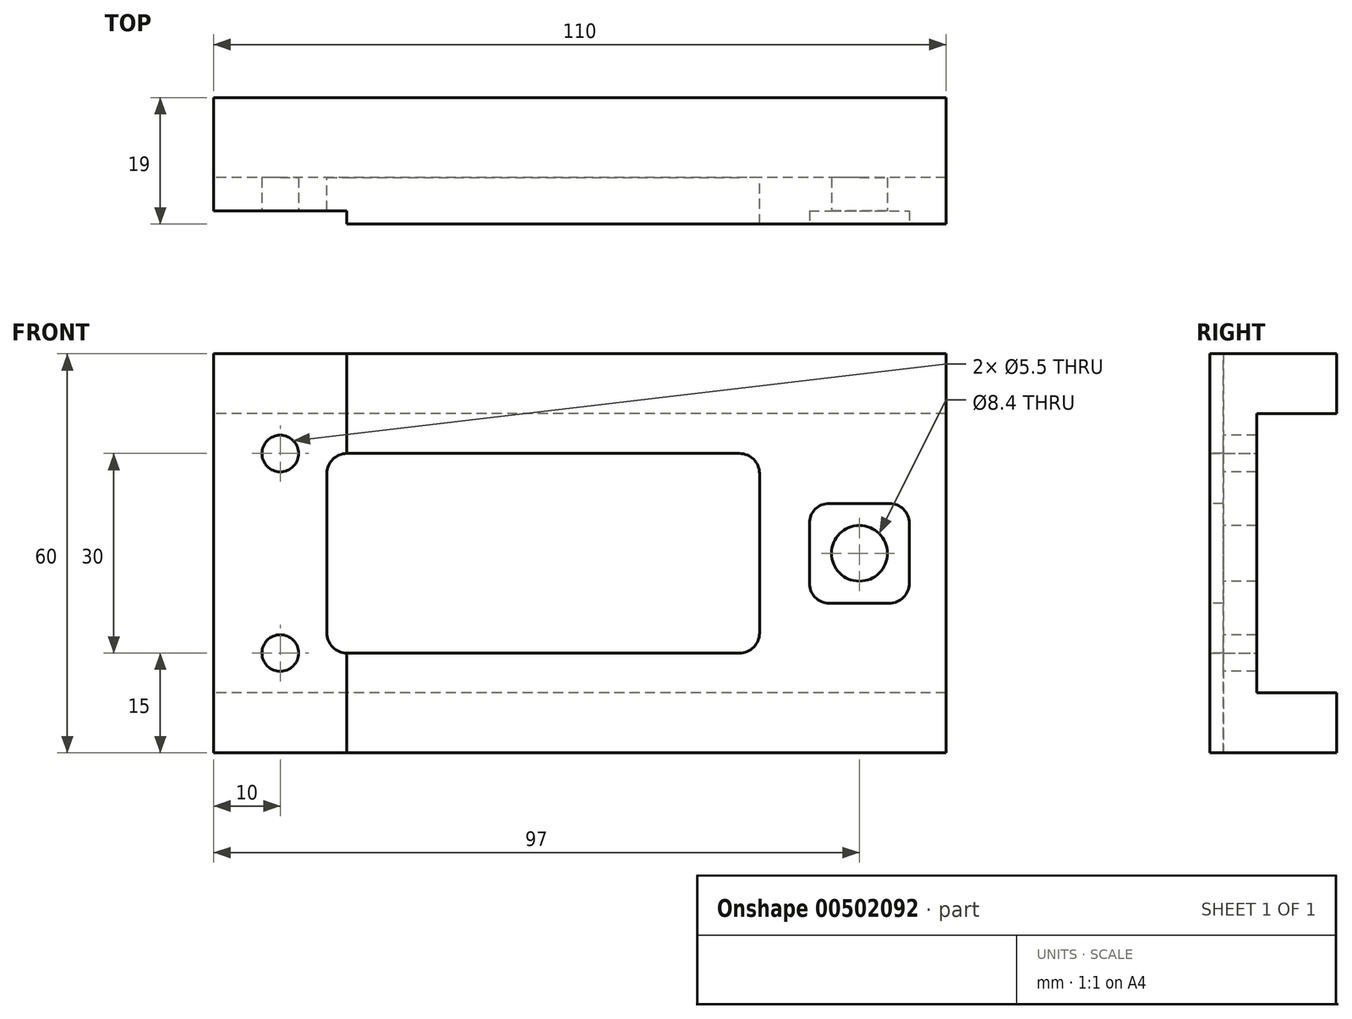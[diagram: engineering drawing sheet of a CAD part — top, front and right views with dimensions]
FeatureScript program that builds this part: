
annotation { "Feature Type Name" : "Feature", "Feature Type Description" : "" }
export const myFeature = defineFeature(function(context is Context, id is Id, definition is map)
    precondition{}
    {
        {
            var Q0;
            Q0=qCreatedBy(makeId("Front.planeOp"),FACE);
            var sketch = newSketch(context, id + "F0", { "sketchPlane" : qUnion([Q0])});
            skLineSegment(sketch, "E0.bottom", {"start": v(0, 0) * mm, "end": v(110, 0) * mm});
            skLineSegment(sketch, "E0.top", {"start": v(0, 60) * mm, "end": v(110, 60) * mm});
            skLineSegment(sketch, "E0.left", {"start": v(0, 0) * mm, "end": v(0, 60) * mm});
            skLineSegment(sketch, "E0.right", {"start": v(110, 0) * mm, "end": v(110, 60) * mm});
            skLineSegment(sketch, "E1.bottom", {"start": v(17, 45) * mm, "end": v(82, 45) * mm});
            skLineSegment(sketch, "E1.top", {"start": v(17, 15) * mm, "end": v(82, 15) * mm});
            skLineSegment(sketch, "E1.left", {"start": v(17, 45) * mm, "end": v(17, 15) * mm});
            skLineSegment(sketch, "E1.right", {"start": v(82, 45) * mm, "end": v(82, 15) * mm});
            skSolve(sketch);
        }
        {
            var Q0;
            Q0=makeQuery(id+"F0.imprint","IMPRINT",FACE,{"disambiguationData":[TD([[makeQuery(id+"F0.imprint","IMPRINT",EDGE,{"derivedFrom":sQuery(id+"F0.wireOp",EDGE,"E0.bottom")}),1.0]])]});
            extrude(context, id + "F1", {"entities" : qUnion([Q0]), "depth" : 19 * mm, "offsetDistance" : 25 * mm});
        }
        {
            var Q0;
            Q0=makeQuery(id+"F1.opExtrude","CAP_FACE",FACE,{"disambiguationData":[OSD([sQuery(id+"F0.wireOp",EDGE,"E0.bottom"),sQuery(id+"F0.wireOp",EDGE,"E0.top"),sQuery(id+"F0.wireOp",EDGE,"E0.left"),sQuery(id+"F0.wireOp",EDGE,"E0.right"),sQuery(id+"F0.wireOp",EDGE,"E1.bottom"),sQuery(id+"F0.wireOp",EDGE,"E1.top"),sQuery(id+"F0.wireOp",EDGE,"E1.left"),sQuery(id+"F0.wireOp",EDGE,"E1.right")])],"isStart":true});
            var sketch = newSketch(context, id + "F2", { "sketchPlane" : qUnion([Q0])});
            skLineSegment(sketch, "E2.bottom", {"start": v(-110, 51) * mm, "end": v(0, 51) * mm});
            skLineSegment(sketch, "E2.top", {"start": v(-110, 9) * mm, "end": v(0, 9) * mm});
            skLineSegment(sketch, "E2.left", {"start": v(-110, 51) * mm, "end": v(-110, 9) * mm});
            skLineSegment(sketch, "E2.right", {"start": v(0, 51) * mm, "end": v(0, 9) * mm});
            skSolve(sketch);
        }
        {
            var Q0;
            Q0=makeQuery(id+"F2.imprint","IMPRINT",FACE,{"disambiguationData":[TD([[makeQuery(id+"F2.imprint","IMPRINT",EDGE,{"derivedFrom":sQuery(id+"F2.wireOp",EDGE,"E2.bottom")}),-1.0]])]});
            extrude(context, id + "F3", {"entities" : qUnion([Q0]), "operationType" : NewBodyOperationType.REMOVE, "oppositeDirection" : true, "depth" : 12 * mm, "offsetDistance" : 25 * mm});
        }
        {
            var Q0;
            Q0=makeQuery(id+"F1.opExtrude","CAP_FACE",FACE,{"disambiguationData":[OSD([sQuery(id+"F0.wireOp",EDGE,"E0.bottom"),sQuery(id+"F0.wireOp",EDGE,"E0.top"),sQuery(id+"F0.wireOp",EDGE,"E0.left"),sQuery(id+"F0.wireOp",EDGE,"E0.right"),sQuery(id+"F0.wireOp",EDGE,"E1.bottom"),sQuery(id+"F0.wireOp",EDGE,"E1.top"),sQuery(id+"F0.wireOp",EDGE,"E1.left"),sQuery(id+"F0.wireOp",EDGE,"E1.right")])],"isStart":false});
            var sketch = newSketch(context, id + "F4", { "sketchPlane" : qUnion([Q0])});
            skLineSegment(sketch, "E3.bottom", {"start": v(0, 60) * mm, "end": v(20, 60) * mm});
            skLineSegment(sketch, "E3.top", {"start": v(0, 0) * mm, "end": v(20, 0) * mm});
            skLineSegment(sketch, "E3.left", {"start": v(0, 60) * mm, "end": v(0, 0) * mm});
            skLineSegment(sketch, "E3.right", {"start": v(20, 60) * mm, "end": v(20, 0) * mm});
            skLineSegment(sketch, "E4.bottom", {"start": v(89.5, 37.5) * mm, "end": v(104.5, 37.5) * mm});
            skLineSegment(sketch, "E4.top", {"start": v(89.5, 22.5) * mm, "end": v(104.5, 22.5) * mm});
            skLineSegment(sketch, "E4.left", {"start": v(89.5, 37.5) * mm, "end": v(89.5, 22.5) * mm});
            skLineSegment(sketch, "E4.right", {"start": v(104.5, 37.5) * mm, "end": v(104.5, 22.5) * mm});
            skSolve(sketch);
        }
        {
            var Q0;
            {var subQ1=sQuery(id+"F4.wireOp",EDGE,"E3.bottom");Q0=makeQuery(id+"F4.imprint","IMPRINT",FACE,{"disambiguationData":[TD([[makeQuery(id+"F4.imprint","IMPRINT",EDGE,{"derivedFrom":subQ1}),-1.0]])]});}
            var Q1;
            Q1=makeQuery(id+"F4.imprint","IMPRINT",FACE,{"disambiguationData":[TD([[makeQuery(id+"F4.imprint","IMPRINT",EDGE,{"derivedFrom":sQuery(id+"F4.wireOp",EDGE,"E4.bottom")}),-1.0]])]});
            extrude(context, id + "F5", {"entities" : qUnion([Q0, Q1]), "operationType" : NewBodyOperationType.REMOVE, "oppositeDirection" : true, "depth" : 2 * mm, "offsetDistance" : 25 * mm});
        }
        {
            var Q0;
            Q0=makeQuery(id+"F1.opExtrude","SWEPT_EDGE",EDGE,{"disambiguationData":[OSD([sQuery(id+"F0.wireOp",EDGE,"E1.bottom"),sQuery(id+"F0.wireOp",EDGE,"E1.left")])]});
            var Q1;
            Q1=makeQuery(id+"F1.opExtrude","SWEPT_EDGE",EDGE,{"disambiguationData":[OSD([sQuery(id+"F0.wireOp",EDGE,"E1.top"),sQuery(id+"F0.wireOp",EDGE,"E1.left")])]});
            var Q2;
            Q2=makeQuery(id+"F1.opExtrude","SWEPT_EDGE",EDGE,{"disambiguationData":[OSD([sQuery(id+"F0.wireOp",EDGE,"E1.bottom"),sQuery(id+"F0.wireOp",EDGE,"E1.right")])]});
            var Q3;
            Q3=makeQuery(id+"F1.opExtrude","SWEPT_EDGE",EDGE,{"disambiguationData":[OSD([sQuery(id+"F0.wireOp",EDGE,"E1.top"),sQuery(id+"F0.wireOp",EDGE,"E1.right")])]});
            var Q4;
            Q4=makeQuery(id+"F5.boolean.opBoolean","COPY",EDGE,{"derivedFrom":makeQuery(id+"F5.opExtrude","SWEPT_EDGE",EDGE,{"disambiguationData":[OSD([sQuery(id+"F4.wireOp",EDGE,"E4.bottom"),sQuery(id+"F4.wireOp",EDGE,"E4.left")])]})});
            var Q5;
            Q5=makeQuery(id+"F5.boolean.opBoolean","COPY",EDGE,{"derivedFrom":makeQuery(id+"F5.opExtrude","SWEPT_EDGE",EDGE,{"disambiguationData":[OSD([sQuery(id+"F4.wireOp",EDGE,"E4.bottom"),sQuery(id+"F4.wireOp",EDGE,"E4.right")])]})});
            var Q6;
            Q6=makeQuery(id+"F5.boolean.opBoolean","COPY",EDGE,{"derivedFrom":makeQuery(id+"F5.opExtrude","SWEPT_EDGE",EDGE,{"disambiguationData":[OSD([sQuery(id+"F4.wireOp",EDGE,"E4.top"),sQuery(id+"F4.wireOp",EDGE,"E4.right")])]})});
            var Q7;
            Q7=makeQuery(id+"F5.boolean.opBoolean","COPY",EDGE,{"derivedFrom":makeQuery(id+"F5.opExtrude","SWEPT_EDGE",EDGE,{"disambiguationData":[OSD([sQuery(id+"F4.wireOp",EDGE,"E4.top"),sQuery(id+"F4.wireOp",EDGE,"E4.left")])]})});
            fillet(context, id + "F6", {"entities" : qUnion([Q0, Q1, Q2, Q3, Q4, Q5, Q6, Q7]), "radius" : 3 * mm, "tangentPropagation" : true, "allowEdgeOverflow" : false});
        }
        {
            var Q0;
            Q0=makeQuery(id+"F5.boolean.opBoolean","COPY",FACE,{"derivedFrom":makeQuery(id+"F5.opExtrude","CAP_FACE",FACE,{"disambiguationData":[OSD([sQuery(id+"F0.wireOp",EDGE,"E1.bottom"),sQuery(id+"F0.wireOp",EDGE,"E1.top"),sQuery(id+"F0.wireOp",EDGE,"E1.left"),sQuery(id+"F4.wireOp",EDGE,"E3.bottom"),sQuery(id+"F4.wireOp",EDGE,"E3.top"),sQuery(id+"F4.wireOp",EDGE,"E3.left"),sQuery(id+"F4.wireOp",EDGE,"E3.right")])],"isStart":false})});
            var sketch = newSketch(context, id + "F7", { "sketchPlane" : qUnion([Q0])});
            skPoint(sketch, "E5", {"position": v(10, 45) * mm});
            skPoint(sketch, "E6", {"position": v(10, 15) * mm});
            skPoint(sketch, "E7", {"position": v(97, 30) * mm});
            skSolve(sketch);
        }
        {
            var Q0;
            Q0=sQuery(id+"F7.wireOp",VERTEX,"E5");
            var Q1;
            Q1=sQuery(id+"F7.wireOp",VERTEX,"E6");
            var Q2;
            Q2=makeQuery(id+"F1.opExtrude","SWEPT_BODY",BODY,{"disambiguationData":[OSD([sQuery(id+"F0.wireOp",EDGE,"E0.bottom"),sQuery(id+"F0.wireOp",EDGE,"E0.top"),sQuery(id+"F0.wireOp",EDGE,"E0.left"),sQuery(id+"F0.wireOp",EDGE,"E0.right"),sQuery(id+"F0.wireOp",EDGE,"E1.bottom"),sQuery(id+"F0.wireOp",EDGE,"E1.top"),sQuery(id+"F0.wireOp",EDGE,"E1.left"),sQuery(id+"F0.wireOp",EDGE,"E1.right")])]});
            hole(context, id + "F8", {"style" : HoleStyle.SIMPLE, "endStyle" : HoleEndStyle.BLIND, "holeDiameter" : 5.5 * mm, "majorDiameter" : 5 * mm, "holeDepth" : 50 * mm, "isTappedThrough" : true, "tappedDepth" : 12 * mm, "tapClearance" : 3, "locations" : qUnion([Q0, Q1]), "scope" : qUnion([Q2])});
        }
        {
            var Q0;
            Q0=sQuery(id+"F7.wireOp",VERTEX,"E7");
            var Q1;
            Q1=makeQuery(id+"F1.opExtrude","SWEPT_BODY",BODY,{"disambiguationData":[OSD([sQuery(id+"F0.wireOp",EDGE,"E0.bottom"),sQuery(id+"F0.wireOp",EDGE,"E0.top"),sQuery(id+"F0.wireOp",EDGE,"E0.left"),sQuery(id+"F0.wireOp",EDGE,"E0.right"),sQuery(id+"F0.wireOp",EDGE,"E1.bottom"),sQuery(id+"F0.wireOp",EDGE,"E1.top"),sQuery(id+"F0.wireOp",EDGE,"E1.left"),sQuery(id+"F0.wireOp",EDGE,"E1.right")])]});
            hole(context, id + "F9", {"style" : HoleStyle.SIMPLE, "endStyle" : HoleEndStyle.BLIND, "holeDiameter" : 8.4 * mm, "majorDiameter" : 5 * mm, "holeDepth" : 50 * mm, "isTappedThrough" : true, "tappedDepth" : 12 * mm, "tapClearance" : 3, "locations" : qUnion([Q0]), "scope" : qUnion([Q1])});
        }
    });
